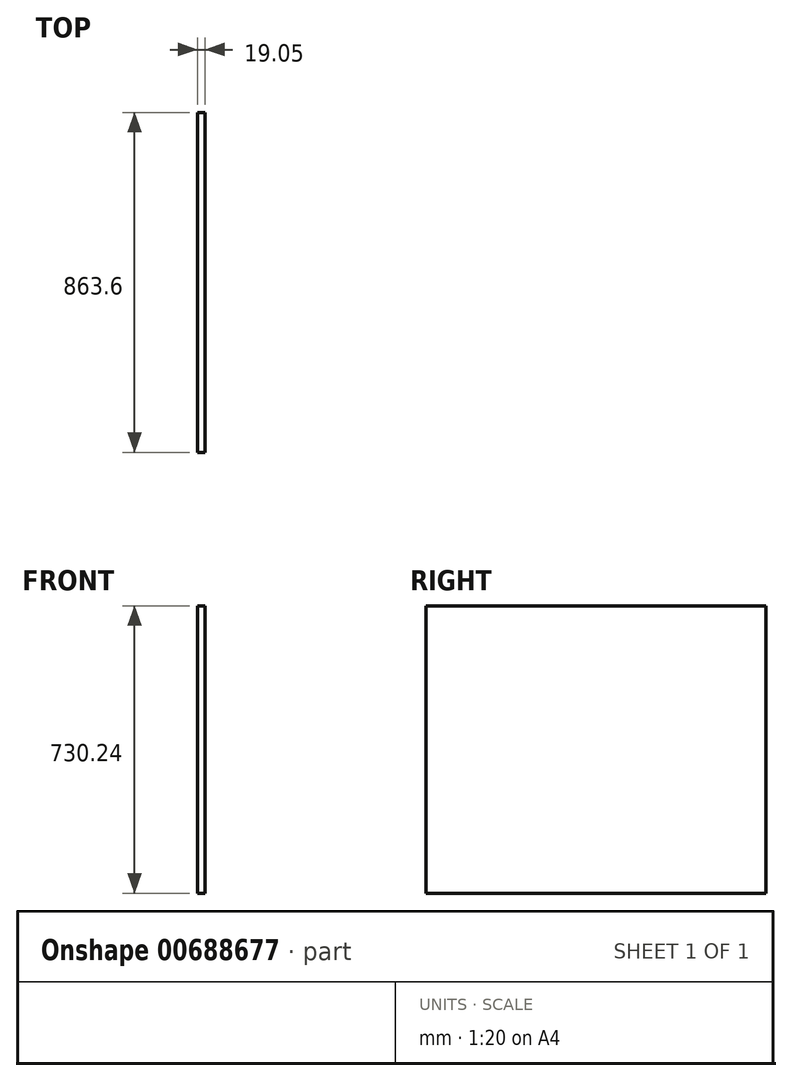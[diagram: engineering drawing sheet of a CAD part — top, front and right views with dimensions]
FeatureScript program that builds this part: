
annotation { "Feature Type Name" : "Feature", "Feature Type Description" : "" }
export const myFeature = defineFeature(function(context is Context, id is Id, definition is map)
    precondition{}
    {
        {
            var Q0;
            Q0=qCreatedBy(makeId("Right.planeOp"),FACE);
            var sketch = newSketch(context, id + "F0", { "sketchPlane" : qUnion([Q0])});
            skLineSegment(sketch, "E0.bottom", {"start": v(431.8, 365.13) * mm, "end": v(-431.8, 365.13) * mm});
            skLineSegment(sketch, "E0.top", {"start": v(431.8, -365.13) * mm, "end": v(-431.8, -365.13) * mm});
            skLineSegment(sketch, "E0.left", {"start": v(431.8, 365.12) * mm, "end": v(431.8, -365.13) * mm});
            skLineSegment(sketch, "E0.right", {"start": v(-431.8, 365.13) * mm, "end": v(-431.8, -365.13) * mm});
            skPoint(sketch, "E0.middle", {"position": v(0, 0) * mm});
            skSolve(sketch);
        }
        {
            var Q0;
            Q0=makeQuery(id+"F0.imprint","IMPRINT",FACE,{"disambiguationData":[TD([[makeQuery(id+"F0.imprint","IMPRINT",EDGE,{"derivedFrom":sQuery(id+"F0.wireOp",EDGE,"E0.bottom")}),1.0]])]});
            extrude(context, id + "F1", {"entities" : qUnion([Q0]), "depth" : 19.05 * mm, "offsetDistance" : 25.4 * mm});
        }
    });
